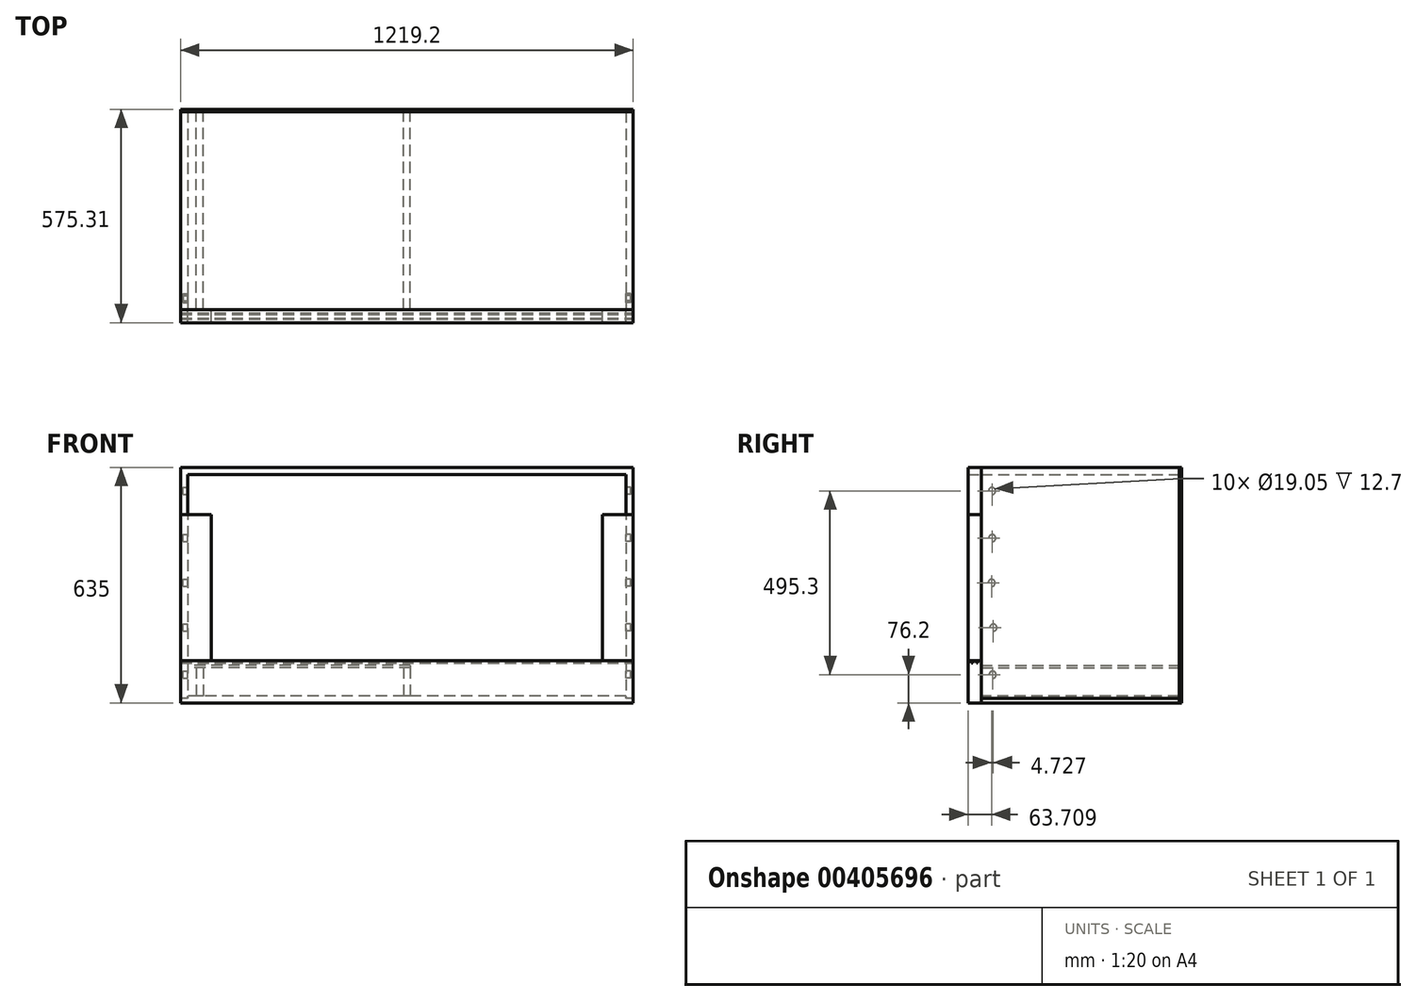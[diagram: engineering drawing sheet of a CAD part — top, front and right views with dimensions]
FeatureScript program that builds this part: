
annotation { "Feature Type Name" : "Feature", "Feature Type Description" : "" }
export const myFeature = defineFeature(function(context is Context, id is Id, definition is map)
    precondition{}
    {
        {
            var Q0;
            Q0=qCreatedBy(makeId("Top.planeOp"),FACE);
            var sketch = newSketch(context, id + "F0", { "sketchPlane" : qUnion([Q0])});
            skLineSegment(sketch, "E0.bottom", {"start": v(609.6, 266.7) * mm, "end": v(-609.6, 266.7) * mm});
            skLineSegment(sketch, "E0.top", {"start": v(609.6, -266.7) * mm, "end": v(-609.6, -266.7) * mm});
            skLineSegment(sketch, "E0.left", {"start": v(609.6, 266.7) * mm, "end": v(609.6, -266.7) * mm});
            skLineSegment(sketch, "E0.right", {"start": v(-609.6, 266.7) * mm, "end": v(-609.6, -266.7) * mm});
            skPoint(sketch, "E0.middle", {"position": v(0, 0) * mm});
            skSolve(sketch);
        }
        {
            var Q0;
            Q0=makeQuery(id+"F0.imprint","IMPRINT",FACE,{"disambiguationData":[TD([[makeQuery(id+"F0.imprint","IMPRINT",EDGE,{"derivedFrom":sQuery(id+"F0.wireOp",EDGE,"E0.bottom")}),1.0]])]});
            extrude(context, id + "F1", {"entities" : qUnion([Q0]), "depth" : 19.05 * mm});
        }
        {
            var Q0;
            Q0=makeQuery(id+"F1.opExtrude","CAP_FACE",FACE,{"disambiguationData":[OSD([sQuery(id+"F0.wireOp",EDGE,"E0.bottom"),sQuery(id+"F0.wireOp",EDGE,"E0.top"),sQuery(id+"F0.wireOp",EDGE,"E0.left"),sQuery(id+"F0.wireOp",EDGE,"E0.right")])],"isStart":false});
            var sketch = newSketch(context, id + "F2", { "sketchPlane" : qUnion([Q0])});
            skLineSegment(sketch, "E1.bottom", {"start": v(-609.6, 266.7) * mm, "end": v(-590.55, 266.7) * mm});
            skLineSegment(sketch, "E1.top", {"start": v(-609.6, -266.7) * mm, "end": v(-590.55, -266.7) * mm});
            skLineSegment(sketch, "E1.left", {"start": v(-609.6, 266.7) * mm, "end": v(-609.6, -266.7) * mm});
            skLineSegment(sketch, "E1.right", {"start": v(-590.55, 266.7) * mm, "end": v(-590.55, -266.7) * mm});
            skLineSegment(sketch, "E2.MirrorCS", {"start": v(609.6, 266.7) * mm, "end": v(590.55, 266.7) * mm});
            skLineSegment(sketch, "E3.MirrorCS", {"start": v(609.6, -266.7) * mm, "end": v(590.55, -266.7) * mm});
            skLineSegment(sketch, "E4.MirrorCS", {"start": v(590.55, 266.7) * mm, "end": v(590.55, -266.7) * mm});
            skLineSegment(sketch, "E5.MirrorCS", {"start": v(609.6, 266.7) * mm, "end": v(609.6, -266.7) * mm});
            skSolve(sketch);
        }
        {
            var Q0;
            Q0=makeQuery(id+"F2.imprint","IMPRINT",FACE,{"disambiguationData":[TD([[makeQuery(id+"F2.imprint","IMPRINT",EDGE,{"derivedFrom":sQuery(id+"F2.wireOp",EDGE,"E1.bottom")}),1.0]])]});
            var Q1;
            Q1=makeQuery(id+"F2.imprint","IMPRINT",FACE,{"disambiguationData":[TD([[makeQuery(id+"F2.imprint","IMPRINT",EDGE,{"derivedFrom":sQuery(id+"F2.wireOp",EDGE,"E2.MirrorCS")}),1.0]])]});
            extrude(context, id + "F3", {"entities" : qUnion([Q0, Q1]), "operationType" : NewBodyOperationType.REMOVE, "oppositeDirection" : true, "depth" : 6.35 * mm});
        }
        {
            var Q0;
            Q0=makeQuery(id+"F3.boolean.opBoolean","COPY",FACE,{"derivedFrom":makeQuery(id+"F3.opExtrude","CAP_FACE",FACE,{"disambiguationData":[OSD([sQuery(id+"F2.wireOp",EDGE,"E1.bottom"),sQuery(id+"F2.wireOp",EDGE,"E1.top"),sQuery(id+"F2.wireOp",EDGE,"E1.left"),sQuery(id+"F2.wireOp",EDGE,"E1.right")])],"isStart":false})});
            var sketch = newSketch(context, id + "F4", { "sketchPlane" : qUnion([Q0])});
            skLineSegment(sketch, "E6.bottom", {"start": v(-609.6, 266.7) * mm, "end": v(-590.55, 266.7) * mm});
            skLineSegment(sketch, "E6.top", {"start": v(-609.6, -266.7) * mm, "end": v(-590.55, -266.7) * mm});
            skLineSegment(sketch, "E6.left", {"start": v(-609.6, 266.7) * mm, "end": v(-609.6, -266.7) * mm});
            skLineSegment(sketch, "E6.right", {"start": v(-590.55, 266.7) * mm, "end": v(-590.55, -266.7) * mm});
            skSolve(sketch);
        }
        {
            var Q0;
            Q0=makeQuery(id+"F4.imprint","IMPRINT",FACE,{"disambiguationData":[TD([[makeQuery(id+"F4.imprint","IMPRINT",EDGE,{"derivedFrom":sQuery(id+"F4.wireOp",EDGE,"E6.bottom")}),1.0]])]});
            extrude(context, id + "F5", {"entities" : qUnion([Q0]), "depth" : 609.6 * mm});
        }
        {
            var Q0;
            Q0=makeQuery(id+"F5.opExtrude","SWEPT_FACE",FACE,{"disambiguationData":[OSD([sQuery(id+"F4.wireOp",EDGE,"E6.right")])]});
            var sketch = newSketch(context, id + "F6", { "sketchPlane" : qUnion([Q0])});
            skCircle(sketch, "E7", {"center": v(-237.37, 571.5) * mm, "radius": 9.53 * mm});
            skCircle(sketch, "E8", {"center": v(-236.7, 444.5) * mm, "radius": 9.53 * mm});
            skCircle(sketch, "E9", {"center": v(-238.55, 323.85) * mm, "radius": 9.53 * mm});
            skCircle(sketch, "E10", {"center": v(-233.82, 203.2) * mm, "radius": 9.53 * mm});
            skCircle(sketch, "E11", {"center": v(-235.75, 76.2) * mm, "radius": 9.53 * mm});
            skSolve(sketch);
        }
        {
            var Q0;
            Q0=makeQuery(id+"F6.imprint","IMPRINT",FACE,{"disambiguationData":[TD([[makeQuery(id+"F6.imprint","IMPRINT",EDGE,{"derivedFrom":sQuery(id+"F6.wireOp",EDGE,"E7")}),1.0]])]});
            var Q1;
            Q1=makeQuery(id+"F6.imprint","IMPRINT",FACE,{"disambiguationData":[TD([[makeQuery(id+"F6.imprint","IMPRINT",EDGE,{"derivedFrom":sQuery(id+"F6.wireOp",EDGE,"E8")}),1.0]])]});
            var Q2;
            Q2=makeQuery(id+"F6.imprint","IMPRINT",FACE,{"disambiguationData":[TD([[makeQuery(id+"F6.imprint","IMPRINT",EDGE,{"derivedFrom":sQuery(id+"F6.wireOp",EDGE,"E10")}),1.0]])]});
            var Q3;
            Q3=makeQuery(id+"F6.imprint","IMPRINT",FACE,{"disambiguationData":[TD([[makeQuery(id+"F6.imprint","IMPRINT",EDGE,{"derivedFrom":sQuery(id+"F6.wireOp",EDGE,"E11")}),1.0]])]});
            var Q4;
            Q4=makeQuery(id+"F6.imprint","IMPRINT",FACE,{"disambiguationData":[TD([[makeQuery(id+"F6.imprint","IMPRINT",EDGE,{"derivedFrom":sQuery(id+"F6.wireOp",EDGE,"E9")}),1.0]])]});
            extrude(context, id + "F7", {"entities" : qUnion([Q0, Q1, Q2, Q3, Q4]), "operationType" : NewBodyOperationType.REMOVE, "oppositeDirection" : true, "depth" : 12.7 * mm});
        }
        {
            var Q0;
            Q0=makeQuery(id+"F5.opExtrude","SWEPT_BODY",BODY,{"disambiguationData":[OSD([sQuery(id+"F4.wireOp",EDGE,"E6.bottom"),sQuery(id+"F4.wireOp",EDGE,"E6.top"),sQuery(id+"F4.wireOp",EDGE,"E6.left"),sQuery(id+"F4.wireOp",EDGE,"E6.right")])]});
            var Q1;
            Q1=qCreatedBy(makeId("Right.planeOp"),FACE);
            mirror(context, id + "F8", {"entities" : qUnion([Q0]), "mirrorPlane" : qUnion([Q1])});
        }
        {
            var Q0;
            Q0=makeQuery(id+"F5.opExtrude","CAP_FACE",FACE,{"disambiguationData":[OSD([sQuery(id+"F4.wireOp",EDGE,"E6.bottom"),sQuery(id+"F4.wireOp",EDGE,"E6.top"),sQuery(id+"F4.wireOp",EDGE,"E6.left"),sQuery(id+"F4.wireOp",EDGE,"E6.right")])],"isStart":false});
            var sketch = newSketch(context, id + "F9", { "sketchPlane" : qUnion([Q0])});
            skLineSegment(sketch, "E12.bottom", {"start": v(-609.6, 266.7) * mm, "end": v(609.6, 266.7) * mm});
            skLineSegment(sketch, "E12.top", {"start": v(-609.6, -266.7) * mm, "end": v(609.6, -266.7) * mm});
            skLineSegment(sketch, "E12.left", {"start": v(-609.6, 266.7) * mm, "end": v(-609.6, -266.7) * mm});
            skLineSegment(sketch, "E12.right", {"start": v(609.6, 266.7) * mm, "end": v(609.6, -266.7) * mm});
            skSolve(sketch);
        }
        {
            var Q0;
            {var subQ0=sQuery(id+"F9.wireOp",EDGE,"E12.left");Q0=makeQuery(id+"F9.imprint","IMPRINT",FACE,{"disambiguationData":[TD([[makeQuery(id+"F9.imprint","IMPRINT",EDGE,{"derivedFrom":subQ0}),1.0]])]});}
            var Q1;
            {var subQ2=sQuery(id+"F9.wireOp",EDGE,"E12.right");Q1=makeQuery(id+"F9.imprint","IMPRINT",FACE,{"disambiguationData":[TD([[makeQuery(id+"F9.imprint","IMPRINT",EDGE,{"derivedFrom":subQ2}),-1.0]])]});}
            extrude(context, id + "F10", {"entities" : qUnion([Q0, Q1]), "depth" : 12.7 * mm});
        }
        {
            var Q0;
            Q0=makeQuery(id+"F10.opExtrude","CAP_FACE",FACE,{"disambiguationData":[OSD([sQuery(id+"F9.wireOp",EDGE,"E12.bottom"),sQuery(id+"F9.wireOp",EDGE,"E12.top"),sQuery(id+"F9.wireOp",EDGE,"E12.left"),sQuery(id+"F9.wireOp",EDGE,"E12.right")])],"isStart":true});
            var sketch = newSketch(context, id + "F11", { "sketchPlane" : qUnion([Q0])});
            skLineSegment(sketch, "E13.bottom", {"start": v(-590.55, 266.7) * mm, "end": v(590.55, 266.7) * mm});
            skLineSegment(sketch, "E13.top", {"start": v(-590.55, -266.7) * mm, "end": v(590.55, -266.7) * mm});
            skLineSegment(sketch, "E13.left", {"start": v(-590.55, 266.7) * mm, "end": v(-590.55, -266.7) * mm});
            skLineSegment(sketch, "E13.right", {"start": v(590.55, 266.7) * mm, "end": v(590.55, -266.7) * mm});
            skSolve(sketch);
        }
        {
            var Q0;
            Q0=makeQuery(id+"F11.imprint","IMPRINT",FACE,{"disambiguationData":[TD([[makeQuery(id+"F11.imprint","IMPRINT",EDGE,{"derivedFrom":sQuery(id+"F11.wireOp",EDGE,"E13.bottom")}),1.0]])]});
            extrude(context, id + "F12", {"entities" : qUnion([Q0]), "operationType" : NewBodyOperationType.ADD, "depth" : 6.35 * mm});
        }
        {
            var Q0;
            Q0=makeQuery(id+"F12.boolean.opBoolean","MERGE",FACE,{"derivedFrom":[makeQuery(id+"F10.opExtrude","SWEPT_FACE",FACE,{"disambiguationData":[OSD([sQuery(id+"F9.wireOp",EDGE,"E12.bottom")])]}),makeQuery(id+"F12.opExtrude","SWEPT_FACE",FACE,{"disambiguationData":[OSD([sQuery(id+"F11.wireOp",EDGE,"E13.top")])]})]});
            var sketch = newSketch(context, id + "F13", { "sketchPlane" : qUnion([Q0])});
            skLineSegment(sketch, "E14.bottom", {"start": v(-609.6, 635) * mm, "end": v(609.6, 635) * mm});
            skLineSegment(sketch, "E14.top", {"start": v(-609.6, 0) * mm, "end": v(609.6, 0) * mm});
            skLineSegment(sketch, "E14.left", {"start": v(-609.6, 635) * mm, "end": v(-609.6, 0) * mm});
            skLineSegment(sketch, "E14.right", {"start": v(609.6, 635) * mm, "end": v(609.6, 0) * mm});
            skSolve(sketch);
        }
        {
            var Q0;
            {var subQ11=sQuery(id+"F13.wireOp",EDGE,"E14.top");Q0=makeQuery(id+"F13.imprint","IMPRINT",FACE,{"disambiguationData":[TD([[makeQuery(id+"F13.imprint","IMPRINT",EDGE,{"derivedFrom":subQ11}),1.0]])]});}
            var Q1;
            {var subQ11=sQuery(id+"F13.wireOp",EDGE,"E14.bottom");Q1=makeQuery(id+"F13.imprint","IMPRINT",FACE,{"disambiguationData":[TD([[makeQuery(id+"F13.imprint","IMPRINT",EDGE,{"derivedFrom":subQ11}),-1.0]])]});}
            extrude(context, id + "F14", {"entities" : qUnion([Q0, Q1]), "depth" : 6.35 * mm});
        }
        {
            var Q0;
            Q0=makeQuery(id+"F1.opExtrude","SWEPT_FACE",FACE,{"disambiguationData":[OSD([sQuery(id+"F0.wireOp",EDGE,"E0.top")])]});
            var sketch = newSketch(context, id + "F15", { "sketchPlane" : qUnion([Q0])});
            skLineSegment(sketch, "E15.bottom", {"start": v(-609.6, 0) * mm, "end": v(609.6, 0) * mm});
            skLineSegment(sketch, "E15.top", {"start": v(-609.6, 114.3) * mm, "end": v(609.6, 114.3) * mm});
            skLineSegment(sketch, "E15.left", {"start": v(-609.6, 0) * mm, "end": v(-609.6, 114.3) * mm});
            skLineSegment(sketch, "E15.right", {"start": v(609.6, 0) * mm, "end": v(609.6, 114.3) * mm});
            skSolve(sketch);
        }
        {
            var Q0;
            {var subQ3=sQuery(id+"F15.wireOp",EDGE,"E15.top");Q0=makeQuery(id+"F15.imprint","IMPRINT",FACE,{"disambiguationData":[TD([[makeQuery(id+"F15.imprint","IMPRINT",EDGE,{"derivedFrom":subQ3}),-1.0]])]});}
            var Q1;
            {var subQ3=sQuery(id+"F15.wireOp",EDGE,"E15.bottom");Q1=makeQuery(id+"F15.imprint","IMPRINT",FACE,{"disambiguationData":[TD([[makeQuery(id+"F15.imprint","IMPRINT",EDGE,{"derivedFrom":subQ3}),-1.0]])]});}
            extrude(context, id + "F16", {"entities" : qUnion([Q0, Q1]), "depth" : 35.56 * mm});
        }
        {
            var Q0;
            Q0=makeQuery(id+"F12.boolean.opBoolean","MERGE",FACE,{"derivedFrom":[makeQuery(id+"F10.opExtrude","SWEPT_FACE",FACE,{"disambiguationData":[OSD([sQuery(id+"F9.wireOp",EDGE,"E12.top")])]}),makeQuery(id+"F12.opExtrude","SWEPT_FACE",FACE,{"disambiguationData":[OSD([sQuery(id+"F11.wireOp",EDGE,"E13.bottom")])]})]});
            var sketch = newSketch(context, id + "F17", { "sketchPlane" : qUnion([Q0])});
            skLineSegment(sketch, "E16.bottom", {"start": v(609.6, 635) * mm, "end": v(-609.6, 635) * mm});
            skLineSegment(sketch, "E16.top", {"start": v(609.6, 508) * mm, "end": v(-609.6, 508) * mm});
            skLineSegment(sketch, "E16.left", {"start": v(609.6, 635) * mm, "end": v(609.6, 508) * mm});
            skLineSegment(sketch, "E16.right", {"start": v(-609.6, 635) * mm, "end": v(-609.6, 508) * mm});
            skSolve(sketch);
        }
        {
            var Q0;
            {var subQ11=sQuery(id+"F17.wireOp",EDGE,"E16.top");Q0=makeQuery(id+"F17.imprint","IMPRINT",FACE,{"disambiguationData":[TD([[makeQuery(id+"F17.imprint","IMPRINT",EDGE,{"derivedFrom":subQ11}),-1.0]])]});}
            var Q1;
            {var subQ11=sQuery(id+"F17.wireOp",EDGE,"E16.bottom");Q1=makeQuery(id+"F17.imprint","IMPRINT",FACE,{"disambiguationData":[TD([[makeQuery(id+"F17.imprint","IMPRINT",EDGE,{"derivedFrom":subQ11}),1.0]])]});}
            extrude(context, id + "F18", {"entities" : qUnion([Q0, Q1]), "depth" : 35.56 * mm});
        }
        {
            var Q0;
            Q0=makeQuery(id+"F5.opExtrude","SWEPT_FACE",FACE,{"disambiguationData":[OSD([sQuery(id+"F4.wireOp",EDGE,"E6.top")])]});
            var sketch = newSketch(context, id + "F19", { "sketchPlane" : qUnion([Q0])});
            skLineSegment(sketch, "E17.bottom", {"start": v(-609.6, 508) * mm, "end": v(-527.05, 508) * mm});
            skLineSegment(sketch, "E17.top", {"start": v(-609.6, 114.3) * mm, "end": v(-527.05, 114.3) * mm});
            skLineSegment(sketch, "E17.left", {"start": v(-609.6, 508) * mm, "end": v(-609.6, 114.3) * mm});
            skLineSegment(sketch, "E17.right", {"start": v(-527.05, 508) * mm, "end": v(-527.05, 114.3) * mm});
            skSolve(sketch);
        }
        {
            var Q0;
            {var subQ0=sQuery(id+"F19.wireOp",EDGE,"E17.right");Q0=makeQuery(id+"F19.imprint","IMPRINT",FACE,{"disambiguationData":[TD([[makeQuery(id+"F19.imprint","IMPRINT",EDGE,{"derivedFrom":subQ0}),-1.0]])]});}
            var Q1;
            {var subQ0=sQuery(id+"F19.wireOp",EDGE,"E17.left");Q1=makeQuery(id+"F19.imprint","IMPRINT",FACE,{"disambiguationData":[TD([[makeQuery(id+"F19.imprint","IMPRINT",EDGE,{"derivedFrom":subQ0}),1.0]])]});}
            extrude(context, id + "F20", {"entities" : qUnion([Q0, Q1]), "depth" : 35.56 * mm});
        }
        {
            var Q0;
            Q0=makeQuery(id+"F20.opExtrude","SWEPT_BODY",BODY,{"disambiguationData":[OSD([sQuery(id+"F19.wireOp",EDGE,"E17.bottom"),sQuery(id+"F19.wireOp",EDGE,"E17.top"),sQuery(id+"F19.wireOp",EDGE,"E17.left"),sQuery(id+"F19.wireOp",EDGE,"E17.right")])]});
            var Q1;
            Q1=qCreatedBy(makeId("Right.planeOp"),FACE);
            mirror(context, id + "F21", {"entities" : qUnion([Q0]), "mirrorPlane" : qUnion([Q1])});
        }
        {
            var Q0;
            Q0=makeQuery(id+"F1.opExtrude","CAP_FACE",FACE,{"disambiguationData":[OSD([sQuery(id+"F0.wireOp",EDGE,"E0.bottom"),sQuery(id+"F0.wireOp",EDGE,"E0.top"),sQuery(id+"F0.wireOp",EDGE,"E0.left"),sQuery(id+"F0.wireOp",EDGE,"E0.right")])],"isStart":false});
            var sketch = newSketch(context, id + "F22", { "sketchPlane" : qUnion([Q0])});
            skLineSegment(sketch, "E18.bottom", {"start": v(-9.52, -266.7) * mm, "end": v(9.52, -266.7) * mm});
            skLineSegment(sketch, "E18.top", {"start": v(-9.52, 266.7) * mm, "end": v(9.52, 266.7) * mm});
            skLineSegment(sketch, "E18.left", {"start": v(-9.52, -266.7) * mm, "end": v(-9.52, 266.7) * mm});
            skLineSegment(sketch, "E18.right", {"start": v(9.52, -266.7) * mm, "end": v(9.52, 266.7) * mm});
            skPoint(sketch, "E19", {"position": v(0, 266.7) * mm});
            skSolve(sketch);
        }
        {
            var Q0;
            Q0=makeQuery(id+"F22.imprint","IMPRINT",FACE,{"disambiguationData":[TD([[makeQuery(id+"F22.imprint","IMPRINT",EDGE,{"derivedFrom":sQuery(id+"F22.wireOp",EDGE,"E18.bottom")}),-1.0]])]});
            var Q1;
            Q1=makeQuery(id+"F16.opExtrude","SWEPT_FACE",FACE,{"disambiguationData":[OSD([sQuery(id+"F15.wireOp",EDGE,"E15.top")])]});
            extrude(context, id + "F23", {"entities" : qUnion([Q0]), "endBoundEntityFace" : qUnion([Q1]), "depth" : 76.2 * mm});
        }
        {
            var Q0;
            Q0=makeQuery(id+"F23.opExtrude","SWEPT_BODY",BODY,{"disambiguationData":[OSD([sQuery(id+"F22.wireOp",EDGE,"E18.bottom"),sQuery(id+"F22.wireOp",EDGE,"E18.top"),sQuery(id+"F22.wireOp",EDGE,"E18.left"),sQuery(id+"F22.wireOp",EDGE,"E18.right")])]});
            transform(context, id + "F24", {"entities" : qUnion([Q0]), "transformType" : TransformType.TRANSLATION_3D, "dx" : -558.8 * mm, "dy" : 0 * mm, "dz" : 0 * mm, "makeCopy" : true});
        }
        {
            var Q0;
            Q0=makeQuery(id+"F23.opExtrude","CAP_FACE",FACE,{"disambiguationData":[OSD([sQuery(id+"F22.wireOp",EDGE,"E18.bottom"),sQuery(id+"F22.wireOp",EDGE,"E18.top"),sQuery(id+"F22.wireOp",EDGE,"E18.left"),sQuery(id+"F22.wireOp",EDGE,"E18.right")])],"isStart":false});
            var sketch = newSketch(context, id + "F25", { "sketchPlane" : qUnion([Q0])});
            skLineSegment(sketch, "E20.bottom", {"start": v(9.53, -266.7) * mm, "end": v(-590.55, -266.7) * mm});
            skLineSegment(sketch, "E20.top", {"start": v(9.52, 266.7) * mm, "end": v(-590.55, 266.7) * mm});
            skLineSegment(sketch, "E20.left", {"start": v(9.52, -266.7) * mm, "end": v(9.52, 266.7) * mm});
            skLineSegment(sketch, "E20.right", {"start": v(-590.55, -266.7) * mm, "end": v(-590.55, 266.7) * mm});
            skSolve(sketch);
        }
        {
            var Q0;
            {var subQ2=sQuery(id+"F25.wireOp",EDGE,"E20.right");Q0=makeQuery(id+"F25.imprint","IMPRINT",FACE,{"disambiguationData":[TD([[makeQuery(id+"F25.imprint","IMPRINT",EDGE,{"derivedFrom":subQ2}),-1.0]])]});}
            var Q1;
            {var subQ0=sQuery(id+"F25.wireOp",EDGE,"E20.left");Q1=makeQuery(id+"F25.imprint","IMPRINT",FACE,{"disambiguationData":[TD([[makeQuery(id+"F25.imprint","IMPRINT",EDGE,{"derivedFrom":subQ0}),1.0]])]});}
            extrude(context, id + "F26", {"entities" : qUnion([Q0, Q1]), "depth" : 6.35 * mm});
        }
        {
            var Q0;
            Q0=makeQuery(id+"F16.opExtrude","SWEPT_FACE",FACE,{"disambiguationData":[OSD([sQuery(id+"F15.wireOp",EDGE,"E15.top")])]});
            var sketch = newSketch(context, id + "F27", { "sketchPlane" : qUnion([Q0])});
            skLineSegment(sketch, "E21.bottom", {"start": v(-609.6, -276.23) * mm, "end": v(609.6, -276.23) * mm});
            skLineSegment(sketch, "E21.top", {"start": v(-609.6, -279.4) * mm, "end": v(609.6, -279.4) * mm});
            skLineSegment(sketch, "E21.left", {"start": v(-609.6, -276.23) * mm, "end": v(-609.6, -279.4) * mm});
            skLineSegment(sketch, "E21.right", {"start": v(609.6, -276.23) * mm, "end": v(609.6, -279.4) * mm});
            skLineSegment(sketch, "E22.bottom", {"start": v(-609.6, -289.56) * mm, "end": v(609.6, -289.56) * mm});
            skLineSegment(sketch, "E22.top", {"start": v(-609.6, -292.74) * mm, "end": v(609.6, -292.74) * mm});
            skLineSegment(sketch, "E22.left", {"start": v(-609.6, -289.56) * mm, "end": v(-609.6, -292.74) * mm});
            skLineSegment(sketch, "E22.right", {"start": v(609.6, -289.56) * mm, "end": v(609.6, -292.74) * mm});
            skSolve(sketch);
        }
        {
            var Q0;
            Q0=makeQuery(id+"F27.imprint","IMPRINT",FACE,{"disambiguationData":[TD([[makeQuery(id+"F27.imprint","IMPRINT",EDGE,{"derivedFrom":sQuery(id+"F27.wireOp",EDGE,"E21.bottom")}),-1.0]])]});
            var Q1;
            Q1=makeQuery(id+"F27.imprint","IMPRINT",FACE,{"disambiguationData":[TD([[makeQuery(id+"F27.imprint","IMPRINT",EDGE,{"derivedFrom":sQuery(id+"F27.wireOp",EDGE,"E22.bottom")}),-1.0]])]});
            extrude(context, id + "F28", {"entities" : qUnion([Q0, Q1]), "operationType" : NewBodyOperationType.REMOVE, "oppositeDirection" : true, "depth" : 6.35 * mm});
        }
    });
